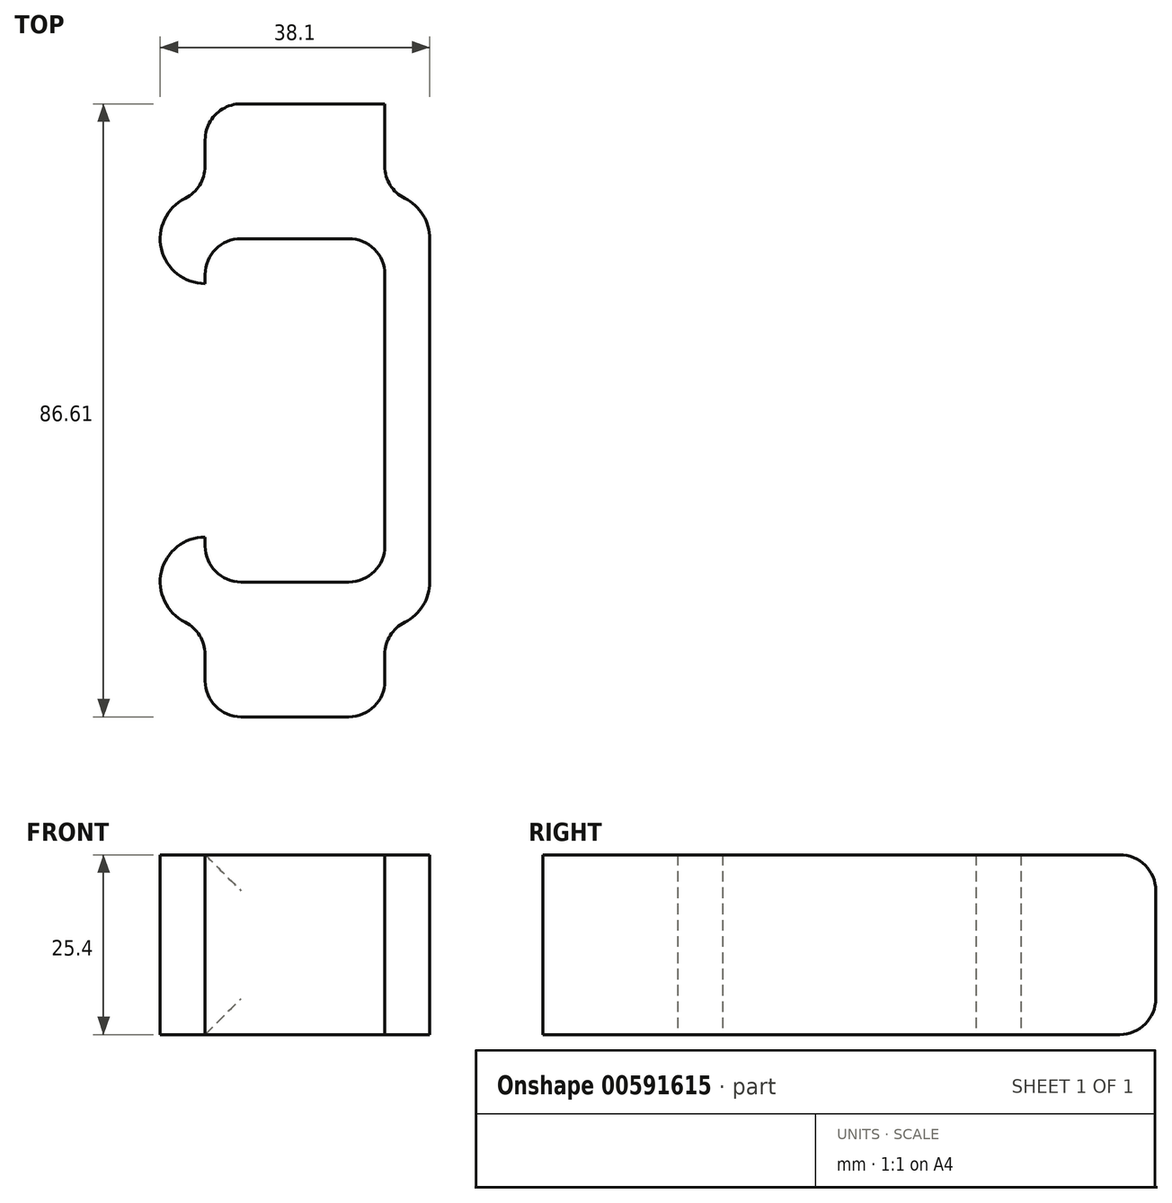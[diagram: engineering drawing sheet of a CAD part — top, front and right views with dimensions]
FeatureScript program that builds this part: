
annotation { "Feature Type Name" : "Feature", "Feature Type Description" : "" }
export const myFeature = defineFeature(function(context is Context, id is Id, definition is map)
    precondition{}
    {
        {
            var Q0;
            Q0=qCreatedBy(makeId("Top.planeOp"),FACE);
            var sketch = newSketch(context, id + "F0", { "sketchPlane" : qUnion([Q0])});
            skLineSegment(sketch, "E0.bottom", {"start": v(-50.04, 11.6) * mm, "end": v(-24.64, 11.6) * mm});
            skLineSegment(sketch, "E0.top", {"start": v(-50.04, 60.1) * mm, "end": v(-24.64, 60.1) * mm});
            skLineSegment(sketch, "E0.left", {"start": v(-50.04, 11.6) * mm, "end": v(-50.04, 17.95) * mm});
            skLineSegment(sketch, "E0.right", {"start": v(-24.64, 11.6) * mm, "end": v(-24.64, 60.1) * mm});
            skArc(sketch, "E1.0.startCap", {"start": v(-50.04, 53.76) * mm, "mid": v(-56.4, 60.1) * mm, "end": v(-50.04, 66.46) * mm});
            skArc(sketch, "E1.0.endCap", {"start": v(-24.64, 66.46) * mm, "mid": v(-20.15, 64.6) * mm, "end": v(-18.3, 60.1) * mm});
            skLineSegment(sketch, "E1.0.left", {"start": v(-50.04, 66.46) * mm, "end": v(-24.64, 66.46) * mm});
            skArc(sketch, "E1.1.startCap", {"start": v(-18.3, 11.6) * mm, "mid": v(-24.64, 5.25) * mm, "end": v(-31, 11.6) * mm});
            skArc(sketch, "E1.1.endCap", {"start": v(-24.64, 66.46) * mm, "mid": v(-20.15, 64.6) * mm, "end": v(-18.3, 60.1) * mm});
            skLineSegment(sketch, "E1.1.right", {"start": v(-18.3, 11.6) * mm, "end": v(-18.3, 60.1) * mm});
            skArc(sketch, "E2.0.startCap", {"start": v(-50.04, 5.25) * mm, "mid": v(-56.4, 11.6) * mm, "end": v(-50.04, 17.95) * mm});
            skArc(sketch, "E2.0.endCap", {"start": v(-18.3, 11.6) * mm, "mid": v(-20.15, 7.11) * mm, "end": v(-24.64, 5.25) * mm});
            skLineSegment(sketch, "E2.0.right", {"start": v(-50.04, 5.25) * mm, "end": v(-24.64, 5.25) * mm});
            skLineSegment(sketch, "E3.trimOffspring", {"start": v(-50.04, 53.76) * mm, "end": v(-50.04, 60.1) * mm});
            skSolve(sketch);
        }
        {
            var Q0;
            {var subQ0=sQuery(id+"F0.wireOp",EDGE,"E1.0.startCap");Q0=makeQuery(id+"F0.imprint","IMPRINT",FACE,{"disambiguationData":[TD([[makeQuery(id+"F0.imprint","IMPRINT",EDGE,{"derivedFrom":subQ0}),-1.0]])]});}
            var Q1;
            {var subQ4=sQuery(id+"F0.wireOp",EDGE,"E1.0.endCap");Q1=makeQuery(id+"F0.imprint","IMPRINT",FACE,{"disambiguationData":[TD([[makeQuery(id+"F0.imprint","IMPRINT",EDGE,{"derivedFrom":subQ4}),-1.0]])]});}
            var Q2;
            {var subQ0=sQuery(id+"F0.wireOp",EDGE,"E1.0.endCap");Q2=makeQuery(id+"F0.imprint","IMPRINT",FACE,{"disambiguationData":[TD([[makeQuery(id+"F0.imprint","IMPRINT",EDGE,{"derivedFrom":subQ0}),1.0]])]});}
            var Q3;
            {var subQ4=sQuery(id+"F0.wireOp",EDGE,"E1.1.startCap");Q3=makeQuery(id+"F0.imprint","IMPRINT",FACE,{"disambiguationData":[TD([[makeQuery(id+"F0.imprint","IMPRINT",EDGE,{"derivedFrom":subQ4}),1.0]])]});}
            var Q4;
            {var subQ6=sQuery(id+"F0.wireOp",EDGE,"E1.1.startCap");Q4=makeQuery(id+"F0.imprint","IMPRINT",FACE,{"disambiguationData":[TD([[makeQuery(id+"F0.imprint","IMPRINT",EDGE,{"derivedFrom":subQ6}),-1.0]])]});}
            extrude(context, id + "F1", {"entities" : qUnion([Q0, Q1, Q2, Q3, Q4]), "depth" : 25.4 * mm, "offsetDistance" : 25.4 * mm});
        }
        {
            var Q0;
            Q0=makeQuery(id+"F1.opExtrude","SWEPT_EDGE",EDGE,{"disambiguationData":[OSD([sQuery(id+"F0.wireOp",EDGE,"E0.bottom"),sQuery(id+"F0.wireOp",EDGE,"E0.right")])]});
            var Q1;
            Q1=makeQuery(id+"F1.opExtrude","SWEPT_EDGE",EDGE,{"disambiguationData":[OSD([sQuery(id+"F0.wireOp",EDGE,"E0.top"),sQuery(id+"F0.wireOp",EDGE,"E0.right")])]});
            var Q2;
            Q2=makeQuery(id+"F1.opExtrude","SWEPT_EDGE",EDGE,{"disambiguationData":[OSD([sQuery(id+"F0.wireOp",EDGE,"E0.top"),sQuery(id+"F0.wireOp",EDGE,"E3.trimOffspring")])]});
            var Q3;
            Q3=makeQuery(id+"F1.opExtrude","SWEPT_EDGE",EDGE,{"disambiguationData":[OSD([sQuery(id+"F0.wireOp",EDGE,"E0.bottom"),sQuery(id+"F0.wireOp",EDGE,"E0.left")])]});
            fillet(context, id + "F2", {"entities" : qUnion([Q0, Q1, Q2, Q3]), "radius" : 5.08 * mm, "tangentPropagation" : true, "allowEdgeOverflow" : false});
        }
        {
            var Q0;
            Q0=makeQuery(id+"F1.opExtrude","SWEPT_FACE",FACE,{"disambiguationData":[OSD([sQuery(id+"F0.wireOp",EDGE,"E1.0.left")])]});
            extrude(context, id + "F3", {"entities" : qUnion([Q0]), "operationType" : NewBodyOperationType.ADD, "depth" : 12.7 * mm, "offsetDistance" : 25.4 * mm});
        }
        {
            var Q0;
            Q0=makeQuery(id+"F1.opExtrude","SWEPT_FACE",FACE,{"disambiguationData":[OSD([sQuery(id+"F0.wireOp",EDGE,"E2.0.right")])]});
            extrude(context, id + "F4", {"entities" : qUnion([Q0]), "operationType" : NewBodyOperationType.ADD, "depth" : 12.7 * mm, "offsetDistance" : 25.4 * mm});
        }
        {
            var Q0;
            Q0=makeQuery(id+"F3.opExtrude","CAP_EDGE",EDGE,{"disambiguationData":[OSD([sQuery(id+"F0.wireOp",EDGE,"E1.0.startCap"),sQuery(id+"F0.wireOp",EDGE,"E1.0.left")])],"isStart":false});
            var Q1;
            Q1=makeQuery(id+"F4.opExtrude","CAP_EDGE",EDGE,{"disambiguationData":[OSD([sQuery(id+"F0.wireOp",EDGE,"E2.0.startCap"),sQuery(id+"F0.wireOp",EDGE,"E2.0.right")])],"isStart":false});
            var Q2;
            {var subQ0=sQuery(id+"F0.wireOp",EDGE,"E2.0.right");var subQ1=sQuery(id+"F0.wireOp",EDGE,"E2.0.startCap");Q2=makeQuery(id+"F4.boolean.opBoolean","MERGE",EDGE,{"derivedFrom":[makeQuery(id+"F1.opExtrude","SWEPT_EDGE",EDGE,{"disambiguationData":[OSD([subQ1,subQ0])]}),makeQuery(id+"F4.opExtrude","CAP_EDGE",EDGE,{"disambiguationData":[OSD([subQ1,subQ0])],"isStart":true})]});}
            var Q3;
            {var subQ0=sQuery(id+"F0.wireOp",EDGE,"E1.0.left");var subQ1=sQuery(id+"F0.wireOp",EDGE,"E1.0.startCap");Q3=makeQuery(id+"F3.boolean.opBoolean","MERGE",EDGE,{"derivedFrom":[makeQuery(id+"F1.opExtrude","SWEPT_EDGE",EDGE,{"disambiguationData":[OSD([subQ1,subQ0])]}),makeQuery(id+"F3.opExtrude","CAP_EDGE",EDGE,{"disambiguationData":[OSD([subQ1,subQ0])],"isStart":true})]});}
            var Q4;
            {var subQ0=sQuery(id+"F0.wireOp",EDGE,"E1.1.endCap");var subQ1=sQuery(id+"F0.wireOp",EDGE,"E1.0.left");Q4=makeQuery(id+"F3.boolean.opBoolean","MERGE",EDGE,{"derivedFrom":[makeQuery(id+"F1.opExtrude","SWEPT_EDGE",EDGE,{"disambiguationData":[OSD([subQ1,subQ0])]}),makeQuery(id+"F3.opExtrude","CAP_EDGE",EDGE,{"disambiguationData":[OSD([subQ1,subQ0])],"isStart":true})]});}
            var Q5;
            Q5=makeQuery(id+"F3.opExtrude","CAP_EDGE",EDGE,{"disambiguationData":[OSD([sQuery(id+"F0.wireOp",EDGE,"E1.0.left"),sQuery(id+"F0.wireOp",EDGE,"E1.1.endCap")])],"isStart":false});
            var Q6;
            Q6=makeQuery(id+"F4.opExtrude","CAP_EDGE",EDGE,{"disambiguationData":[OSD([sQuery(id+"F0.wireOp",EDGE,"E1.1.startCap"),sQuery(id+"F0.wireOp",EDGE,"E2.0.endCap"),sQuery(id+"F0.wireOp",EDGE,"E2.0.right")])],"isStart":false});
            var Q7;
            {var subQ0=sQuery(id+"F0.wireOp",EDGE,"E2.0.right");var subQ1=sQuery(id+"F0.wireOp",EDGE,"E2.0.endCap");var subQ2=sQuery(id+"F0.wireOp",EDGE,"E1.1.startCap");Q7=makeQuery(id+"F4.boolean.opBoolean","MERGE",EDGE,{"derivedFrom":[makeQuery(id+"F1.opExtrude","SWEPT_EDGE",EDGE,{"disambiguationData":[OSD([subQ2,subQ1,subQ0])]}),makeQuery(id+"F4.opExtrude","CAP_EDGE",EDGE,{"disambiguationData":[OSD([subQ2,subQ1,subQ0])],"isStart":true})]});}
            fillet(context, id + "F5", {"entities" : qUnion([Q0, Q1, Q2, Q3, Q4, Q5, Q6, Q7]), "radius" : 5.08 * mm, "tangentPropagation" : true, "allowEdgeOverflow" : false});
        }
    });
